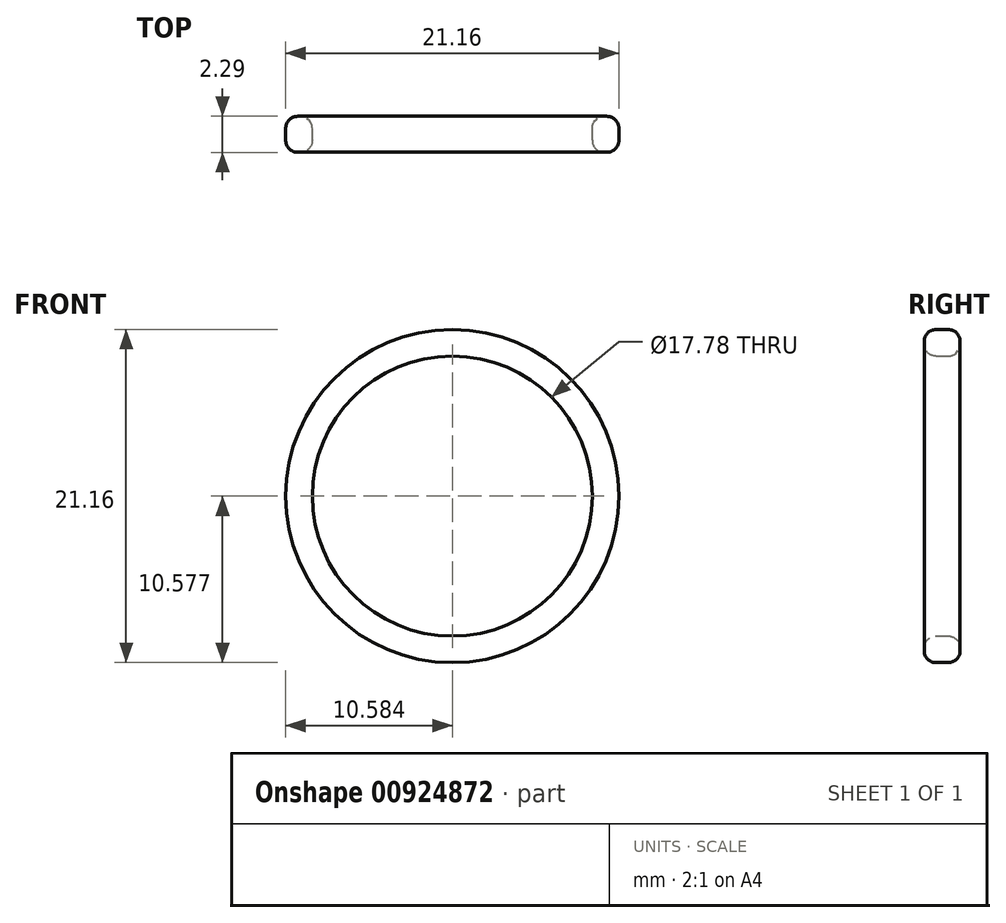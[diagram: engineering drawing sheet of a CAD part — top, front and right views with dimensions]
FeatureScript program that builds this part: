
annotation { "Feature Type Name" : "Feature", "Feature Type Description" : "" }
export const myFeature = defineFeature(function(context is Context, id is Id, definition is map)
    precondition{}
    {
        {
            var Q0;
            Q0=qCreatedBy(makeId("Front.planeOp"),FACE);
            var sketch = newSketch(context, id + "F0", { "sketchPlane" : qUnion([Q0])});
            skCircle(sketch, "E0", {"center": v(-48, 41) * mm, "radius": 8.9 * mm});
            skCircle(sketch, "E1", {"center": v(-48, 41) * mm, "radius": 10.58 * mm});
            skSolve(sketch);
        }
        {
            var Q0;
            Q0=makeQuery(id+"F0.imprint","IMPRINT",FACE,{"disambiguationData":[TD([[makeQuery(id+"F0.imprint","IMPRINT",EDGE,{"derivedFrom":sQuery(id+"F0.wireOp",EDGE,"E0")}),-1.0]])]});
            extrude(context, id + "F1", {"entities" : qUnion([Q0]), "depth" : 2.3 * mm, "offsetDistance" : 25.4 * mm});
        }
        {
            var Q0;
            Q0=makeQuery(id+"F1.opExtrude","CAP_EDGE",EDGE,{"disambiguationData":[OSD([sQuery(id+"F0.wireOp",EDGE,"E1")])],"isStart":false});
            var Q1;
            Q1=makeQuery(id+"F1.opExtrude","CAP_EDGE",EDGE,{"disambiguationData":[OSD([sQuery(id+"F0.wireOp",EDGE,"E1")])],"isStart":true});
            var Q2;
            Q2=makeQuery(id+"F1.opExtrude","CAP_EDGE",EDGE,{"disambiguationData":[OSD([sQuery(id+"F0.wireOp",EDGE,"E0")])],"isStart":true});
            var Q3;
            Q3=makeQuery(id+"F1.opExtrude","CAP_EDGE",EDGE,{"disambiguationData":[OSD([sQuery(id+"F0.wireOp",EDGE,"E0")])],"isStart":false});
            fillet(context, id + "F2", {"entities" : qUnion([Q0, Q1, Q2, Q3]), "radius" : 0.76 * mm, "tangentPropagation" : true, "allowEdgeOverflow" : false});
        }
    });
